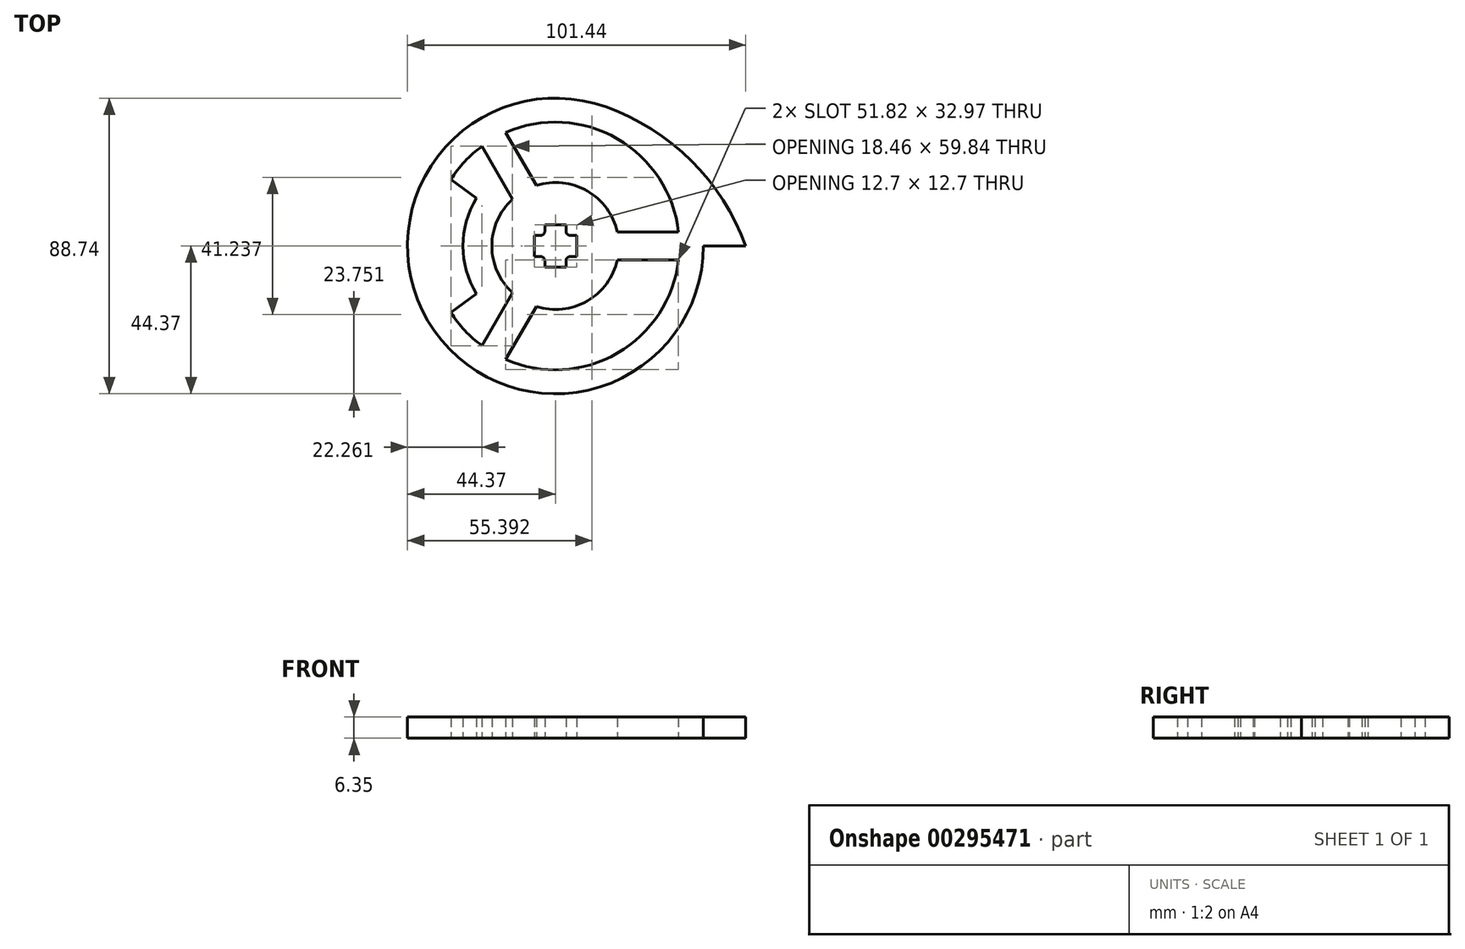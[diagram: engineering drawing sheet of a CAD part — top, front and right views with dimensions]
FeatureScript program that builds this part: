
annotation { "Feature Type Name" : "Feature", "Feature Type Description" : "" }
export const myFeature = defineFeature(function(context is Context, id is Id, definition is map)
    precondition{}
    {
        {
            var Q0;
            Q0=qCreatedBy(makeId("Top.planeOp"),FACE);
            var sketch = newSketch(context, id + "F0", { "sketchPlane" : qUnion([Q0])});
            skCircle(sketch, "E0", {"center": v(0, 0) * mm, "radius": 19.05 * mm});
            skLineSegment(sketch, "E1.bottom", {"start": v(3.18, 6.35) * mm, "end": v(-3.17, 6.35) * mm});
            skLineSegment(sketch, "E1.top", {"start": v(3.17, -6.35) * mm, "end": v(-3.18, -6.35) * mm});
            skLineSegment(sketch, "E1.left", {"start": v(3.18, 6.35) * mm, "end": v(3.17, -6.35) * mm});
            skLineSegment(sketch, "E1.right", {"start": v(-3.17, 6.35) * mm, "end": v(-3.18, -6.35) * mm});
            skLineSegment(sketch, "E2.bottom", {"start": v(6.35, 3.18) * mm, "end": v(-6.35, 3.18) * mm});
            skLineSegment(sketch, "E2.top", {"start": v(6.35, -3.18) * mm, "end": v(-6.35, -3.18) * mm});
            skLineSegment(sketch, "E2.left", {"start": v(6.35, 3.18) * mm, "end": v(6.35, -3.18) * mm});
            skLineSegment(sketch, "E2.right", {"start": v(-6.35, 3.18) * mm, "end": v(-6.35, -3.18) * mm});
            skCircle(sketch, "E3", {"center": v(0, 0) * mm, "radius": 37.16 * mm});
            skCircle(sketch, "E4", {"center": v(0, 0) * mm, "radius": 44.37 * mm});
            skLineSegment(sketch, "E5", {"start": v(18.6, 4.13) * mm, "end": v(36.93, 4.13) * mm});
            skLineSegment(sketch, "E6", {"start": v(19.05, 0) * mm, "end": v(13.54, 0) * mm});
            skPoint(sketch, "E6.startSnap0", {"position": v(6.35, 0) * mm});
            skPoint(sketch, "E6.endSnap0", {"position": v(6.35, 0) * mm});
            skLineSegment(sketch, "E7.MirrorCS", {"start": v(18.6, -4.13) * mm, "end": v(36.93, -4.13) * mm});
            skLineSegment(sketch, "E8.1.0", {"start": v(-12.88, 14.04) * mm, "end": v(-22.04, 29.92) * mm});
            skLineSegment(sketch, "E8.1.1", {"start": v(-5.72, 18.17) * mm, "end": v(-14.89, 34.05) * mm});
            skLineSegment(sketch, "E8.1.2", {"start": v(-9.52, 16.5) * mm, "end": v(-6.77, 11.72) * mm});
            skLineSegment(sketch, "E8.2.0", {"start": v(-5.72, -18.17) * mm, "end": v(-14.89, -34.05) * mm});
            skLineSegment(sketch, "E8.2.1", {"start": v(-12.88, -14.04) * mm, "end": v(-22.04, -29.92) * mm});
            skLineSegment(sketch, "E8.2.2", {"start": v(-9.53, -16.5) * mm, "end": v(-6.77, -11.72) * mm});
            skLineSegment(sketch, "E9", {"start": v(44.37, 0) * mm, "end": v(57.07, 0) * mm});
            skArc(sketch, "E10", {"start": v(57.07, 0) * mm, "mid": v(40.78, 25.58) * mm, "end": v(15.1, 41.72) * mm});
            skCircle(sketch, "E11", {"center": v(0, 0) * mm, "radius": 27.7 * mm});
            skLineSegment(sketch, "E12", {"start": v(-23.68, -14.38) * mm, "end": v(-31.34, -19.97) * mm});
            skLineSegment(sketch, "E13.MirrorCS", {"start": v(-23.68, 14.38) * mm, "end": v(-31.34, 19.97) * mm});
            skSolve(sketch);
        }
        {
            var Q0;
            Q0 = qSketchRegion(id + "F0", true);
            var Q1;
            {var subQ0=sQuery(id+"F0.wireOp",EDGE,"E8.1.0");Q1=makeQuery(id+"F0.imprint","IMPRINT",FACE,{"disambiguationData":[TD([[makeQuery(id+"F0.imprint","IMPRINT",EDGE,{"derivedFrom":subQ0}),-1.0]])]});}
            var Q2;
            {var subQ0=sQuery(id+"F0.wireOp",EDGE,"E8.2.0");Q2=makeQuery(id+"F0.imprint","IMPRINT",FACE,{"disambiguationData":[TD([[makeQuery(id+"F0.imprint","IMPRINT",EDGE,{"derivedFrom":subQ0}),-1.0]])]});}
            var Q3;
            {var subQ0=sQuery(id+"F0.wireOp",EDGE,"E5");Q3=makeQuery(id+"F0.imprint","IMPRINT",FACE,{"disambiguationData":[TD([[makeQuery(id+"F0.imprint","IMPRINT",EDGE,{"derivedFrom":subQ0}),-1.0]])]});}
            var Q4;
            {var subQ0=sQuery(id+"F0.wireOp",EDGE,"E1.bottom");Q4=makeQuery(id+"F0.imprint","IMPRINT",FACE,{"disambiguationData":[TD([[makeQuery(id+"F0.imprint","IMPRINT",EDGE,{"derivedFrom":subQ0}),-1.0]])]});}
            var Q5;
            {var subQ1=sQuery(id+"F0.wireOp",EDGE,"E0");var subQ8=makeQuery(id+"F0.imprint","IMPRINT",VERTEX,{"disambiguationData":[OD(1.0)],"derivedFrom":subQ1});Q5=makeQuery(id+"F0.imprint","IMPRINT",FACE,{"disambiguationData":[TD([[makeQuery(id+"F0.imprint","IMPRINT",EDGE,{"disambiguationData":[TD([[subQ8,1.0]])],"derivedFrom":subQ1}),-1.0]])]});}
            var Q6;
            {var subQ1=sQuery(id+"F0.wireOp",EDGE,"E0");var subQ5=makeQuery(id+"F0.imprint","IMPRINT",VERTEX,{"disambiguationData":[OD(0.0)],"derivedFrom":subQ1});Q6=makeQuery(id+"F0.imprint","IMPRINT",FACE,{"disambiguationData":[TD([[makeQuery(id+"F0.imprint","IMPRINT",EDGE,{"disambiguationData":[TD([[subQ5,-1.0]])],"derivedFrom":subQ1}),-1.0]])]});}
            var Q7;
            {var subQ1=sQuery(id+"F0.wireOp",EDGE,"E0");var subQ7=makeQuery(id+"F0.imprint","IMPRINT",VERTEX,{"disambiguationData":[OD(2.0)],"derivedFrom":subQ1});Q7=makeQuery(id+"F0.imprint","IMPRINT",FACE,{"disambiguationData":[TD([[makeQuery(id+"F0.imprint","IMPRINT",EDGE,{"disambiguationData":[TD([[subQ7,1.0]])],"derivedFrom":subQ1}),-1.0]])]});}
            var Q8;
            {var subQ0=sQuery(id+"F0.wireOp",EDGE,"E12");Q8=makeQuery(id+"F0.imprint","IMPRINT",FACE,{"disambiguationData":[TD([[makeQuery(id+"F0.imprint","IMPRINT",EDGE,{"derivedFrom":subQ0}),-1.0]])]});}
            extrude(context, id + "F1", {"entities" : qUnion([Q0, Q1, Q2, Q3, Q4, Q5, Q6, Q7, Q8]), "depth" : 6.35 * mm});
        }
        {
            var Q0;
            Q0=makeQuery(id+"F1.opExtrude","SWEPT_EDGE",EDGE,{"disambiguationData":[OSD([sQuery(id+"F0.wireOp",EDGE,"E1.right"),sQuery(id+"F0.wireOp",EDGE,"E2.bottom")])]});
            var Q1;
            Q1=makeQuery(id+"F1.opExtrude","SWEPT_EDGE",EDGE,{"disambiguationData":[OSD([sQuery(id+"F0.wireOp",EDGE,"E1.right"),sQuery(id+"F0.wireOp",EDGE,"E2.top")])]});
            var Q2;
            Q2=makeQuery(id+"F1.opExtrude","SWEPT_EDGE",EDGE,{"disambiguationData":[OSD([sQuery(id+"F0.wireOp",EDGE,"E1.left"),sQuery(id+"F0.wireOp",EDGE,"E2.top")])]});
            var Q3;
            Q3=makeQuery(id+"F1.opExtrude","SWEPT_EDGE",EDGE,{"disambiguationData":[OSD([sQuery(id+"F0.wireOp",EDGE,"E1.left"),sQuery(id+"F0.wireOp",EDGE,"E2.bottom")])]});
            fillet(context, id + "F2", {"entities" : qUnion([Q0, Q1, Q2, Q3]), "radius" : 1.27 * mm, "tangentPropagation" : true, "allowEdgeOverflow" : false});
        }
    });
